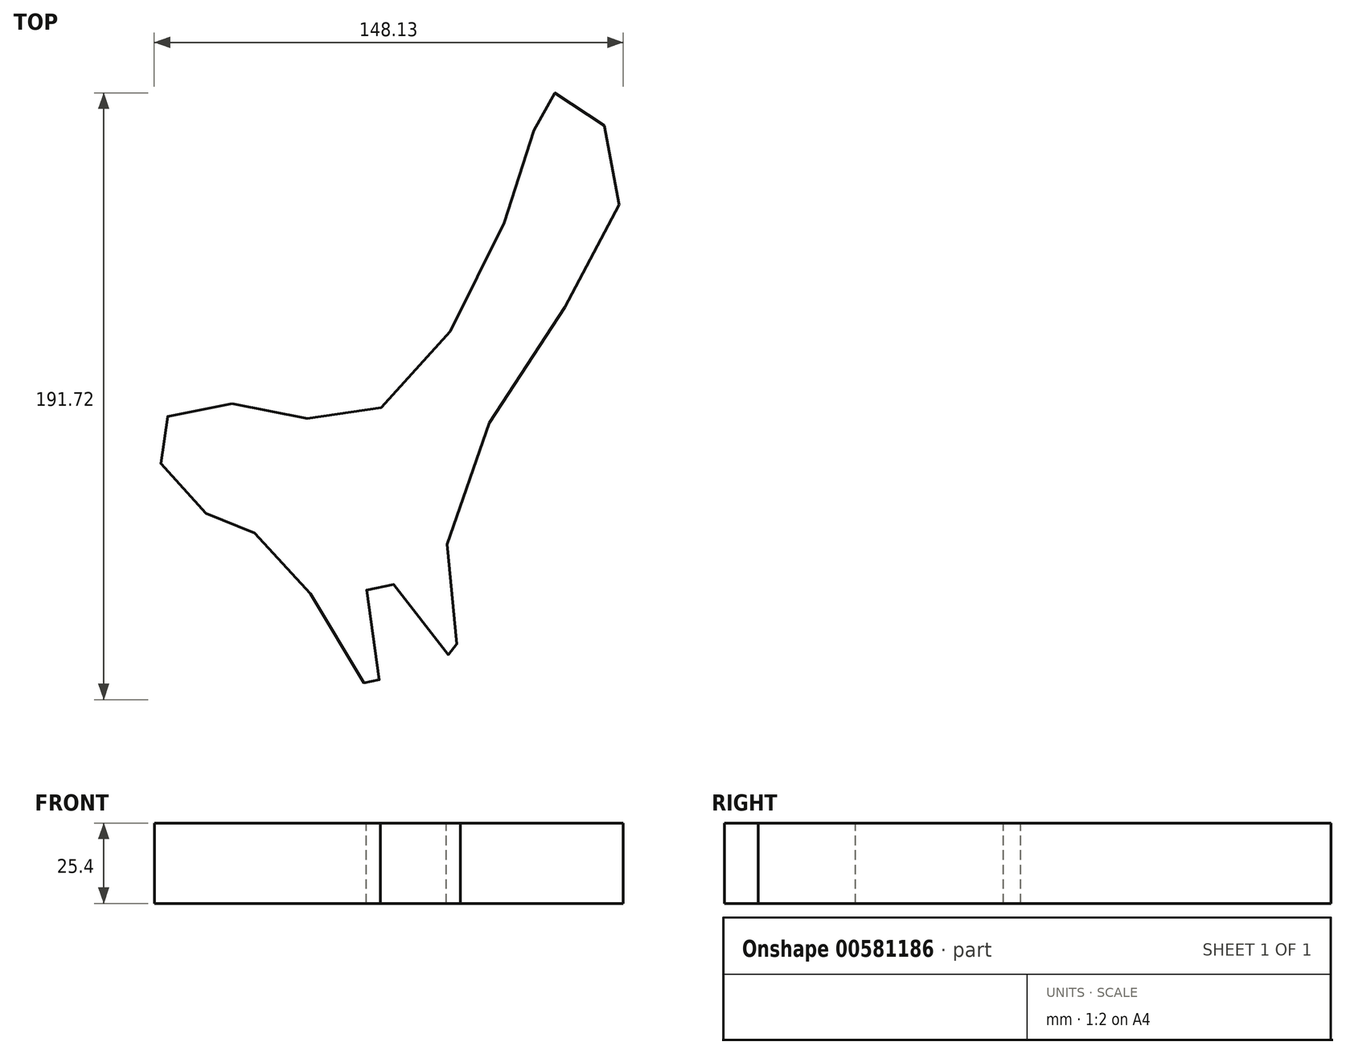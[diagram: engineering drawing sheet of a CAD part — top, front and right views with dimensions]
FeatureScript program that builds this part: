
annotation { "Feature Type Name" : "Feature", "Feature Type Description" : "" }
export const myFeature = defineFeature(function(context is Context, id is Id, definition is map)
    precondition{}
    {
        {
            var Q0;
            Q0=qCreatedBy(makeId("Top.planeOp"),FACE);
            var sketch = newSketch(context, id + "F0", { "sketchPlane" : qUnion([Q0])});
            skFitSpline(sketch, "E0", {"points": [v(-174.43, -179.91) * mm, v(-129, -182.05) * mm, v(-80.94, -100.83) * mm, v(-72.35, -81.68) * mm, v(-50.9, -107.5) * mm, v(-105.68, -217.7) * mm, v(-103.43, -262.25) * mm, v(-130.65, -232.12) * mm, v(-127.77, -273.02) * mm, v(-159.33, -226.86) * mm, v(-182.07, -214.88) * mm, v(-198.83, -189.63) * mm, v(-174.43, -179.91) * mm]});
            skSolve(sketch);
        }
        {
            var Q0;
            Q0=sQuery(id+"F0.wireOp",EDGE,"E0");
            extrude(context, id + "F1", {"bodyType" : ToolBodyType.SURFACE, "surfaceEntities" : qUnion([Q0]), "depth" : 25.4 * mm, "offsetDistance" : 25.4 * mm});
        }
    });
